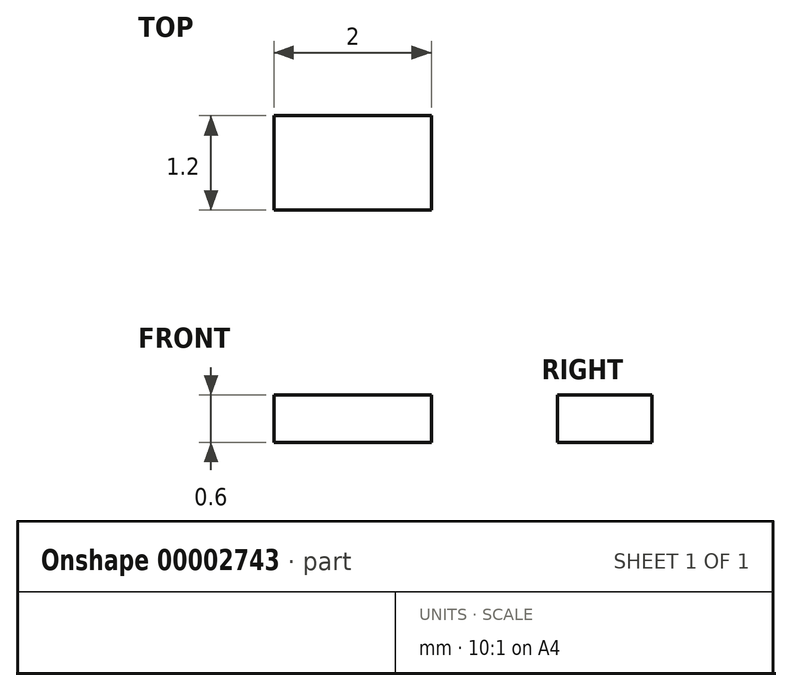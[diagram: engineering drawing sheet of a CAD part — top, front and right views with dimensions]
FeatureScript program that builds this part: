
annotation { "Feature Type Name" : "Feature", "Feature Type Description" : "" }
export const myFeature = defineFeature(function(context is Context, id is Id, definition is map)
    precondition{}
    {
        {
            var Q0;
            Q0=qCreatedBy(makeId("Top.planeOp"),FACE);
            var sketch = newSketch(context, id + "F0", { "sketchPlane" : qUnion([Q0])});
            skLineSegment(sketch, "E0.bottom", {"start": v(2.31, 0.02) * mm, "end": v(4.31, 0.02) * mm});
            skLineSegment(sketch, "E0.top", {"start": v(2.31, -1.18) * mm, "end": v(4.31, -1.18) * mm});
            skLineSegment(sketch, "E0.left", {"start": v(2.31, 0.02) * mm, "end": v(2.31, -1.18) * mm});
            skLineSegment(sketch, "E0.right", {"start": v(4.31, 0.02) * mm, "end": v(4.31, -1.18) * mm});
            skSolve(sketch);
        }
        {
            var Q0;
            Q0=makeQuery(id+"F0.imprint","IMPRINT",FACE,{"disambiguationData":[TD([[makeQuery(id+"F0.imprint","IMPRINT",EDGE,{"derivedFrom":sQuery(id+"F0.wireOp",EDGE,"E0.bottom")}),-1.0]])]});
            extrude(context, id + "F1", {"entities" : qUnion([Q0]), "depth" : .6 * mm});
        }
    });
